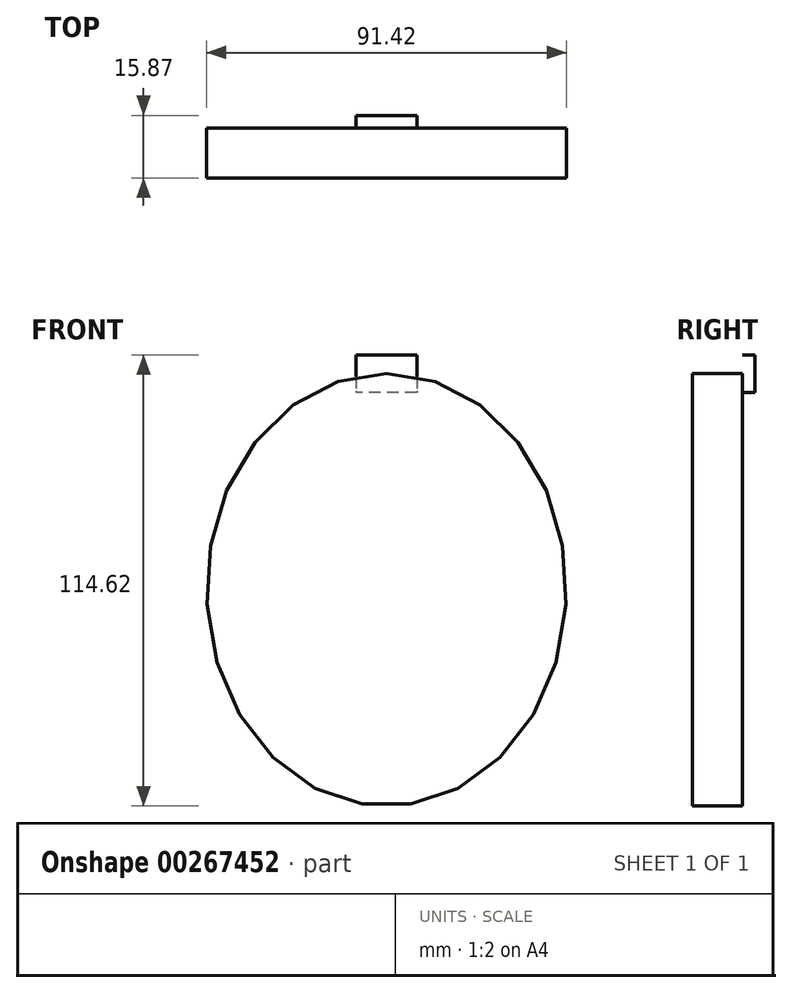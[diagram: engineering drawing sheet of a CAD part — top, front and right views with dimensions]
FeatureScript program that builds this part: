
annotation { "Feature Type Name" : "Feature", "Feature Type Description" : "" }
export const myFeature = defineFeature(function(context is Context, id is Id, definition is map)
    precondition{}
    {
        {
            var Q0;
            Q0=qCreatedBy(makeId("Front.planeOp"),FACE);
            var sketch = newSketch(context, id + "F0", { "sketchPlane" : qUnion([Q0])});
            skEllipse(sketch, "E0", {"center": v(0, 0) * mm, "majorRadius": 54.94 * mm, "minorRadius": 45.7 * mm, "majorAxis": v(0, 1)});
            skLineSegment(sketch, "E1.bottom", {"start": v(7.7, 59.68) * mm, "end": v(-7.7, 59.68) * mm});
            skLineSegment(sketch, "E1.top", {"start": v(7.7, 50.2) * mm, "end": v(-7.7, 50.2) * mm});
            skLineSegment(sketch, "E1.left", {"start": v(7.7, 59.68) * mm, "end": v(7.7, 50.2) * mm});
            skLineSegment(sketch, "E1.right", {"start": v(-7.7, 59.68) * mm, "end": v(-7.7, 50.2) * mm});
            skPoint(sketch, "E1.middle", {"position": v(0, 54.94) * mm});
            skLineSegment(sketch, "E2.top", {"start": v(7.7, 44) * mm, "end": v(-7.7, 44) * mm});
            skLineSegment(sketch, "E2.left", {"start": v(7.7, 50.2) * mm, "end": v(7.7, 44) * mm});
            skLineSegment(sketch, "E2.right", {"start": v(-7.7, 50.2) * mm, "end": v(-7.7, 44) * mm});
            skPoint(sketch, "E2.middle", {"position": v(0, 47.1) * mm});
            skSolve(sketch);
        }
        {
            var Q0;
            Q0=makeQuery(id+"F0.imprint","IMPRINT",FACE,{"disambiguationData":[TD([[makeQuery(id+"F0.imprint","IMPRINT",EDGE,{"derivedFrom":sQuery(id+"F0.wireOp",EDGE,"E0")}),1.0]])]});
            var Q1;
            Q1=makeQuery(id+"F0.imprint","IMPRINT",FACE,{"disambiguationData":[TD([[makeQuery(id+"F0.imprint","IMPRINT",EDGE,{"derivedFrom":sQuery(id+"F0.wireOp",EDGE,"IE47pfZi-XIrK-4fCM-yOkF-zG5R4P9R5vRQ")}),-1.0]])]});
            var Q2;
            Q2=makeQuery(id+"F0.imprint","IMPRINT",FACE,{"disambiguationData":[TD([[makeQuery(id+"F0.imprint","IMPRINT",EDGE,{"derivedFrom":sQuery(id+"F0.wireOp",EDGE,"E1.top")}),1.0]])]});
            var Q3;
            Q3=makeQuery(id+"F0.imprint","IMPRINT",FACE,{"disambiguationData":[TD([[makeQuery(id+"F0.imprint","IMPRINT",EDGE,{"derivedFrom":sQuery(id+"F0.wireOp",EDGE,"E2.top")}),1.0]])]});
            extrude(context, id + "F1", {"entities" : qUnion([Q0, Q1, Q2, Q3]), "depth" : 12.7 * mm});
        }
        {
            var Q0;
            {var subQ5=sQuery(id+"F0.wireOp",EDGE,"E1.bottom");Q0=makeQuery(id+"F0.imprint","IMPRINT",FACE,{"disambiguationData":[TD([[makeQuery(id+"F0.imprint","IMPRINT",EDGE,{"derivedFrom":subQ5}),1.0]])]});}
            var Q1;
            {var subQ5=sQuery(id+"F0.wireOp",EDGE,"E1.top");Q1=makeQuery(id+"F0.imprint","IMPRINT",FACE,{"disambiguationData":[TD([[makeQuery(id+"F0.imprint","IMPRINT",EDGE,{"derivedFrom":subQ5}),-1.0]])]});}
            extrude(context, id + "F2", {"entities" : qUnion([Q0, Q1]), "oppositeDirection" : true, "depth" : 3.17 * mm});
        }
    });
